# Revit family: Domotics-DomesticRanges-GEWISS-SYSTEM_POWER-SOCKET-OUTLET_SELV_POLARIZED
name_source: partatom
category: Apparecchi elettrici
revit_build: Autodesk Revit 2016 (Build: 20161004_0715(x64)
units: mm (PartAtom-declared; Revit-internal decimal feet)

## family parameters
Condiviso = Sì
Host = Superficie
Mantenere orientamento annotazione = Sì
Punto di calcolo locali = Sì
Quota connettore circolare = Usa diametro
Taglio con vuoti quando caricato = Sì
Tipo di parte = Normale

## types (2) — shared parameters
Carico apparente = 0 VA
Catalogue = DOMOTICS
Catalogue Range = SYSTEM - DOMESTIC RANGE
Centre distance = 12,4MM
Description: = 2P - 6A - 24V polarized
Electrocod = 0131
For plug pins = Flat
IDF = f2a6a854-6efa-437d-af86-69526c3383e4
IDT = 4b18969e-7d95-4a3a-aefc-ed383d35ebe9
Immagine tipo = GW21234.jpg
N. poli = 1
No. SYSTEM modules = 1
Produttore = GEWISS S.p.A.
Prospetto di default = 1219 mm
SEO = Socket outlet
Technical sheet = https://www.gewiss.com
Tipo_ = SYSTEM PRESE SELV_GENERICO : GW21234 Presa 2P 6A 24V (SELV) polarizzata nero
URL = https://www.gewiss.com
Version file RFA = 19.4
Volt = 230 V

## per-type parameters (varying)
| type | Colour | Descrizione | EAN code | Modello |
| GW20234 - USA-POLARIZED PHONE SOCKET OUTLET SY/WT | White | USA-POLARIZED PHONE SOCKET OUTLET SY/WT | 8011564000766 | GW20234 |
| GW21234 - USA-POLARIZED PHONE SOCKET OUTLET SY/BK | Black | USA-POLARIZED PHONE SOCKET OUTLET SY/BK | 8011564128774 | GW21234 |

## geometry (parser evidence)
native form markers: Sweep x2
no freeform markers — native parametric forms only
